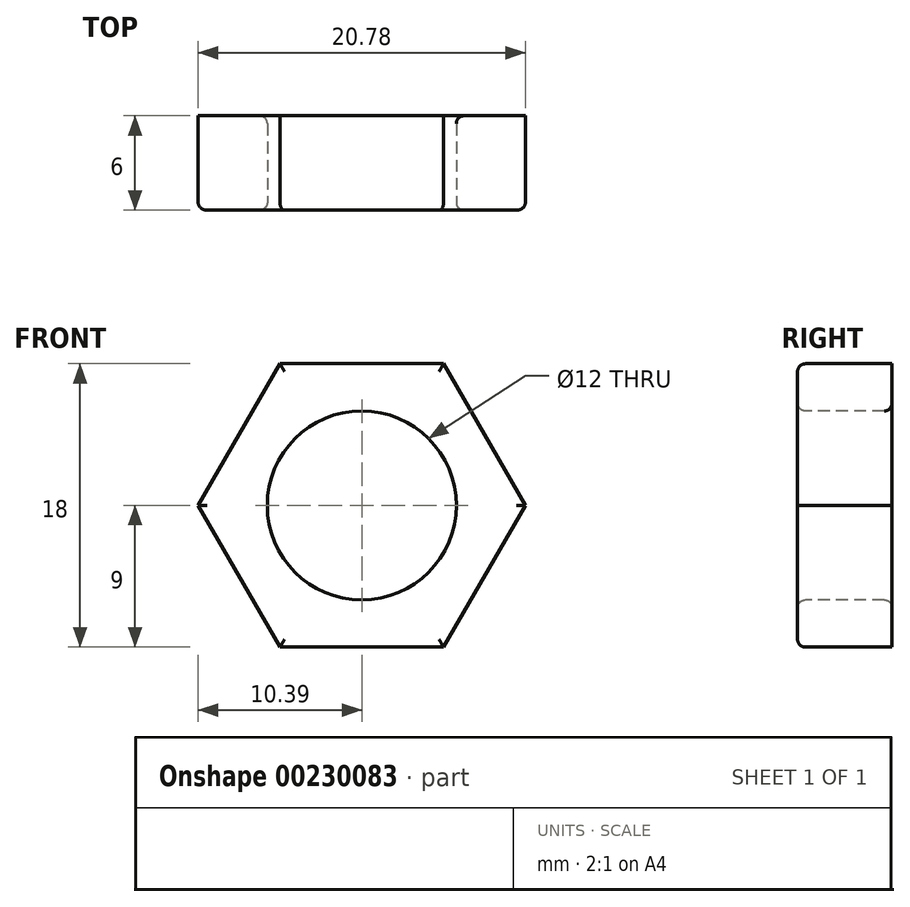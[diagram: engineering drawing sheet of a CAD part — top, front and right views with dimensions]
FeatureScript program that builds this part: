
annotation { "Feature Type Name" : "Feature", "Feature Type Description" : "" }
export const myFeature = defineFeature(function(context is Context, id is Id, definition is map)
    precondition{}
    {
        {
            var Q0;
            Q0=qCreatedBy(makeId("Front.planeOp"),FACE);
            var sketch = newSketch(context, id + "F0", { "sketchPlane" : qUnion([Q0])});
            skCircle(sketch, "E0.cCircle", {"center": v(0, 0) * mm, "radius": 9 * mm, "construction": true});
            skLineSegment(sketch, "E0.0", {"start": v(-5.2, 9) * mm, "end": v(5.2, 9) * mm});
            skLineSegment(sketch, "E0.1", {"start": v(5.2, 9) * mm, "end": v(10.4, 0) * mm});
            skLineSegment(sketch, "E0.2", {"start": v(10.4, 0) * mm, "end": v(5.2, -9) * mm});
            skLineSegment(sketch, "E0.3", {"start": v(5.2, -9) * mm, "end": v(-5.2, -9) * mm});
            skLineSegment(sketch, "E0.4", {"start": v(-5.2, -9) * mm, "end": v(-10.4, 0) * mm});
            skLineSegment(sketch, "E0.5", {"start": v(-10.4, 0) * mm, "end": v(-5.2, 9) * mm});
            skPoint(sketch, "E0.0.midPoint", {"position": v(0, 9) * mm});
            skSolve(sketch);
        }
        {
            var Q0;
            Q0 = qSketchRegion(id + "F0", true);
            extrude(context, id + "F1", {"entities" : qUnion([Q0]), "depth" : 6 * mm});
        }
        {
            var Q0;
            Q0=makeQuery(id+"F1.opExtrude","CAP_FACE",FACE,{"disambiguationData":[OSD([sQuery(id+"F0.wireOp",EDGE,"E0.0"),sQuery(id+"F0.wireOp",EDGE,"E0.1"),sQuery(id+"F0.wireOp",EDGE,"E0.2"),sQuery(id+"F0.wireOp",EDGE,"E0.3"),sQuery(id+"F0.wireOp",EDGE,"E0.4"),sQuery(id+"F0.wireOp",EDGE,"E0.5")])],"isStart":false});
            var sketch = newSketch(context, id + "F2", { "sketchPlane" : qUnion([Q0])});
            skCircle(sketch, "E1", {"center": v(0, 0) * mm, "radius": 6 * mm});
            skSolve(sketch);
        }
        {
            var Q0;
            Q0 = qSketchRegion(id + "F2", true);
            extrude(context, id + "F3", {"entities" : qUnion([Q0]), "operationType" : NewBodyOperationType.REMOVE, "oppositeDirection" : true, "depth" : 25 * mm});
        }
        {
            var Q0;
            Q0=makeQuery(id+"F1.opExtrude","CAP_FACE",FACE,{"disambiguationData":[OSD([sQuery(id+"F0.wireOp",EDGE,"E0.0"),sQuery(id+"F0.wireOp",EDGE,"E0.1"),sQuery(id+"F0.wireOp",EDGE,"E0.2"),sQuery(id+"F0.wireOp",EDGE,"E0.3"),sQuery(id+"F0.wireOp",EDGE,"E0.4"),sQuery(id+"F0.wireOp",EDGE,"E0.5")])],"isStart":false});
            var Q1;
            Q1=makeQuery(id+"F3.boolean.opBoolean","INTERSECT",EDGE,{"derivedFrom":[makeQuery(id+"F1.opExtrude","CAP_FACE",FACE,{"disambiguationData":[OSD([sQuery(id+"F0.wireOp",EDGE,"E0.0"),sQuery(id+"F0.wireOp",EDGE,"E0.1"),sQuery(id+"F0.wireOp",EDGE,"E0.2"),sQuery(id+"F0.wireOp",EDGE,"E0.3"),sQuery(id+"F0.wireOp",EDGE,"E0.4"),sQuery(id+"F0.wireOp",EDGE,"E0.5")])],"isStart":true}),makeQuery(id+"F3.opExtrude","SWEPT_FACE",FACE,{"disambiguationData":[OSD([sQuery(id+"F2.wireOp",EDGE,"E1")])]})]});
            fillet(context, id + "F4", {"entities" : qUnion([Q0, Q1]), "radius" : .5 * mm, "tangentPropagation" : true, "allowEdgeOverflow" : false});
        }
    });
